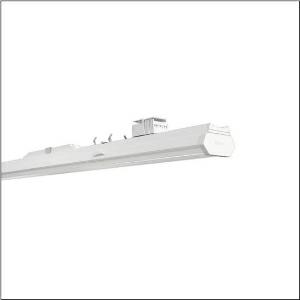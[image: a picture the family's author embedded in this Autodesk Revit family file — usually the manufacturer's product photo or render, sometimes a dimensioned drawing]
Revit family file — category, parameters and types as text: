
# Revit family: licross_21_protected_ho_52td1bdn4d5m
name_source: partatom
category: Lighting Fixtures
units: mm (PartAtom-declared; Revit-internal decimal feet)

## family parameters
Cut with Voids When Loaded = No
Host = Face
Light Source = No
Part Type = Normal
Room Calculation Point = No
Round Connector Dimension = Use Diameter
Shared = No

## types (1)
- --- (1 x LED, 13950 lm, 84.9 W, 4000K)
    Apparent Load = 85 VA
    CIE Flux Codes = 54 82 95 97 100
    Color Rendering = 80
    Color Temperature = 4000K
    Default Elevation = 1800 mm
    Description = Licross 21 Protected HO, luminaire insert, of sheet steel, galvanised, coil coated, white, length: 1.500mm, width: 90mm, height: 103mm, LED rated luminous flux: 13.950lm, light colour: 840, SDCM (Standard Deviation of Colour Matching)MacAdam ≤ 3 SDCM (initial), control gear: DALI 2, with plug, 5-pole, with phase selection, mains connection: 220..240V, AC, 50/60Hz, rated input power: 85W, internal wiring halogen-free, primary optical cover: cover, of PMMA, light emission: direct distribution, primary light characteristic: symmetric, protection rating (complete): IP54, insulation class (complete): insulation class I (protective earthing), certification: CE, ENEC, VDE, UKCA, protection symbol: D if used in an environment with non-conductive dust loads with corresponding accessories, impact resistance: IK06, permissible ambient temperature for indoor applications: -25..+35°C, corresponds to IFS (International Featured Standards) requirements for safety and quality in the food industry, reducing of maximum allowable ambient temperature of 5°C with ceiling mounting, LABS conformity tested according to VDMA 24364:2018-05, The light source and the operating device comply with the requirements of the Ecodesign Regulation (EU) 2019/2020 and are replaceable in accordance with this regulation, packaging unit: 1 piece
    Height = 92 mm
    Lamp = 1 x LED
    Lamp Light Flux = 13950 lm
    Lamp Power = 84.9 W
    Lamp count = 1
    Length = 1500 mm
    Luminous efficacy = 164 lm/W
    Manufacturer = Siteco
    ModVariant = No
    Model = 52TD1BDN4D5M
    Mounting Place = Ceiling
    Mounting Type = Pendant
    Number of Poles = 1
    OnlyDefault = Yes
    Power Factor = 1
    Product Name = Licross 21 Protected HO
    Product group = luminaire insert | ceiling pendant
    ProductGroupID = 901
    Protection Class = Protection class I
    Protection Degree = IP 54
    RLX_Detail_Level = 1
    RLX_Emergency_Light_Flux = 0 lm
    RLX_Emergency_Type = 0
    RLX_Emergency_Type_DB = No
    RlxData = <blob elided: 24577 chars, md5=5ea71149>
    Socket = socket
    Standby Power = 0 W
    System Light Flux = 13950 lm
    System Power = 85 W
    Type Comments = factory setting: luminous flux: 100 % | dim-lin: 254 | 484 mA
    Type Image = l_1256148.jpg
    URL = http://relux.com
    VarID = @adj_129263
    Voltage = 0 V
    Weight = 0.00 kg
    Width = 88 mm

## geometry (parser evidence)
native form markers: Blend x4, Sweep x12
no freeform markers — native parametric forms only
